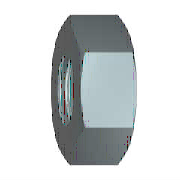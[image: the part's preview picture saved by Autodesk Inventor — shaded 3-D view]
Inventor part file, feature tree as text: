
AUTODESK INVENTOR PART (.ipt)
format: ipt  version: 2015 (Build 190159000, 159)  size: 171,520 bytes
history: native  units: mm (DEFAULTED — no unit token found)
features: sketch x3, chamfer x1, hole x1, other x1, plane x1
ambient origin geometry x7: Origin, YZ Plane, XZ Plane, X Axis, Y Axis, Z Axis, Center Point
bodies: Solid1 (feature_tree), Body (feature_tree)
feature tree (7):
  chamfer  "Chamfer1"  Angle=30.0deg  [1 undecoded]
  hole  "Thread"  [1 undecoded]
  other  "Work Axis1"
  plane  "Work Plane1"
  sketch  "Sketch1"  dims[d0=12.83161mm]
  sketch  "Sketch2"  dims[d1=5.5626mm]
  sketch  "Sketch3"  dims[d2=0.0mm d3=30.0deg d4=30.0deg d5=11.1125mm d6=11.1125mm d7=90.0deg d25=4.9784mm d26=6.0mm d27=4.0mm d28=2.0mm d29=14.3117mm d30=8.0mm d31=20.594885mm d8=0.687408mm d9=30.0deg d10=0.687408mm d11=30.0deg d13=0.0mm d14=0.0mm d39=0.0mm d40=0.687408mm d41=0.687408mm d42=0.0mm]
note: 2 required parameter values undecoded (feature->parameter linkage not recoverable at this tier; creation-order binding heuristic only, values carry confidence <= 0.55)
